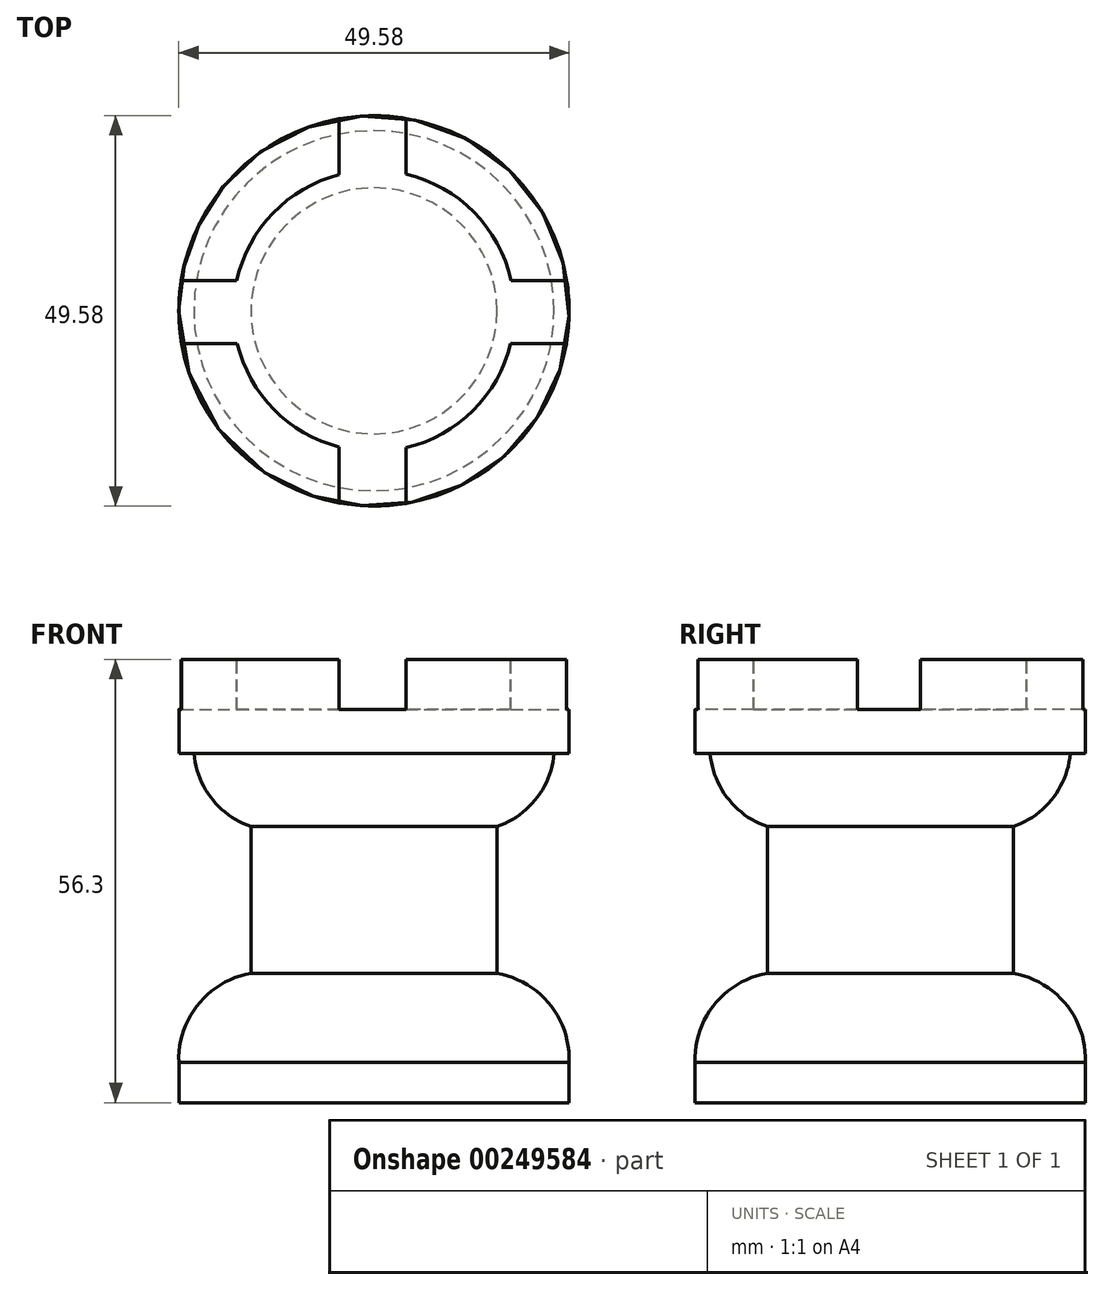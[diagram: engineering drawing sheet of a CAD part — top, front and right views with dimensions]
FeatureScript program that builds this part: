
annotation { "Feature Type Name" : "Feature", "Feature Type Description" : "" }
export const myFeature = defineFeature(function(context is Context, id is Id, definition is map)
    precondition{}
    {
        {
            var Q0;
            Q0=qCreatedBy(makeId("Front.planeOp"),FACE);
            var sketch = newSketch(context, id + "F0", { "sketchPlane" : qUnion([Q0])});
            skLineSegment(sketch, "E0", {"start": v(0, 0) * mm, "end": v(0, 56.3) * mm});
            skLineSegment(sketch, "E1", {"start": v(0, 56.3) * mm, "end": v(-24.78, 56.3) * mm});
            skLineSegment(sketch, "E2", {"start": v(-24.78, 56.3) * mm, "end": v(-24.78, 44.34) * mm});
            skLineSegment(sketch, "E3", {"start": v(-24.78, 0) * mm, "end": v(0, 0) * mm});
            skArc(sketch, "E4", {"start": v(-15.62, 16.43) * mm, "mid": v(-22.33, 12.5) * mm, "end": v(-24.78, 5.12) * mm});
            skLineSegment(sketch, "E5", {"start": v(-15.62, 16.43) * mm, "end": v(-15.62, 35.07) * mm});
            skArc(sketch, "E6", {"start": v(-22.87, 44.36) * mm, "mid": v(-20.62, 38.65) * mm, "end": v(-15.62, 35.07) * mm});
            skLineSegment(sketch, "E7", {"start": v(-22.87, 44.36) * mm, "end": v(-24.78, 44.34) * mm});
            skLineSegment(sketch, "E8.trimOffspring", {"start": v(-24.78, 5.12) * mm, "end": v(-24.78, 0) * mm});
            skSolve(sketch);
        }
        {
            var Q0;
            Q0=makeQuery(id+"F0.imprint","IMPRINT",FACE,{"disambiguationData":[TD([[makeQuery(id+"F0.imprint","IMPRINT",EDGE,{"derivedFrom":sQuery(id+"F0.wireOp",EDGE,"E0")}),1.0]])]});
            var Q1;
            Q1=sQuery(id+"F0.wireOp",EDGE,"E0");
            revolve(context, id + "F1", {"entities" : qUnion([Q0]), "axis" : qUnion([Q1]), "revolveType" : RevolveType.FULL});
        }
        {
            var Q0;
            Q0=makeQuery(id+"F1.opRevolve","SWEPT_FACE",FACE,{"disambiguationData":[OSD([sQuery(id+"F0.wireOp",EDGE,"E1")])]});
            var sketch = newSketch(context, id + "F2", { "sketchPlane" : qUnion([Q0])});
            skLineSegment(sketch, "E9.bottom", {"start": v(-4.42, 25.96) * mm, "end": v(4.07, 25.96) * mm});
            skLineSegment(sketch, "E9.top", {"start": v(-4.42, -27.86) * mm, "end": v(4.07, -27.86) * mm});
            skLineSegment(sketch, "E9.left", {"start": v(-4.42, 25.96) * mm, "end": v(-4.42, -27.86) * mm});
            skLineSegment(sketch, "E9.right", {"start": v(4.07, 25.96) * mm, "end": v(4.07, -27.86) * mm});
            skLineSegment(sketch, "E10.bottom", {"start": v(-28.28, 3.86) * mm, "end": v(30.18, 3.86) * mm});
            skLineSegment(sketch, "E10.top", {"start": v(-28.28, -4.15) * mm, "end": v(30.18, -4.15) * mm});
            skLineSegment(sketch, "E10.left", {"start": v(-28.28, 3.86) * mm, "end": v(-28.28, -4.15) * mm});
            skLineSegment(sketch, "E10.right", {"start": v(30.18, 3.86) * mm, "end": v(30.18, -4.15) * mm});
            skCircle(sketch, "E11", {"center": v(0, 0) * mm, "radius": 17.85 * mm});
            skSolve(sketch);
        }
        {
            var Q0;
            Q0 = qSketchRegion(id + "F2", true);
            var Q1;
            {var subQ0=sQuery(id+"F2.wireOp",EDGE,"E10.bottom");var subQ1=sQuery(id+"F2.wireOp",EDGE,"E9.left");var subQ2=makeQuery(id+"F2.imprint","INTERSECT",VERTEX,{"derivedFrom":[subQ1,subQ0]});Q1=makeQuery(id+"F2.imprint","IMPRINT",FACE,{"disambiguationData":[TD([[makeQuery(id+"F2.imprint","IMPRINT",EDGE,{"disambiguationData":[TD([[subQ2,-1.0]])],"derivedFrom":subQ1}),1.0]])]});}
            extrude(context, id + "F3", {"entities" : qUnion([Q0, Q1]), "operationType" : NewBodyOperationType.REMOVE, "oppositeDirection" : true, "depth" : 6.35 * mm});
        }
    });
